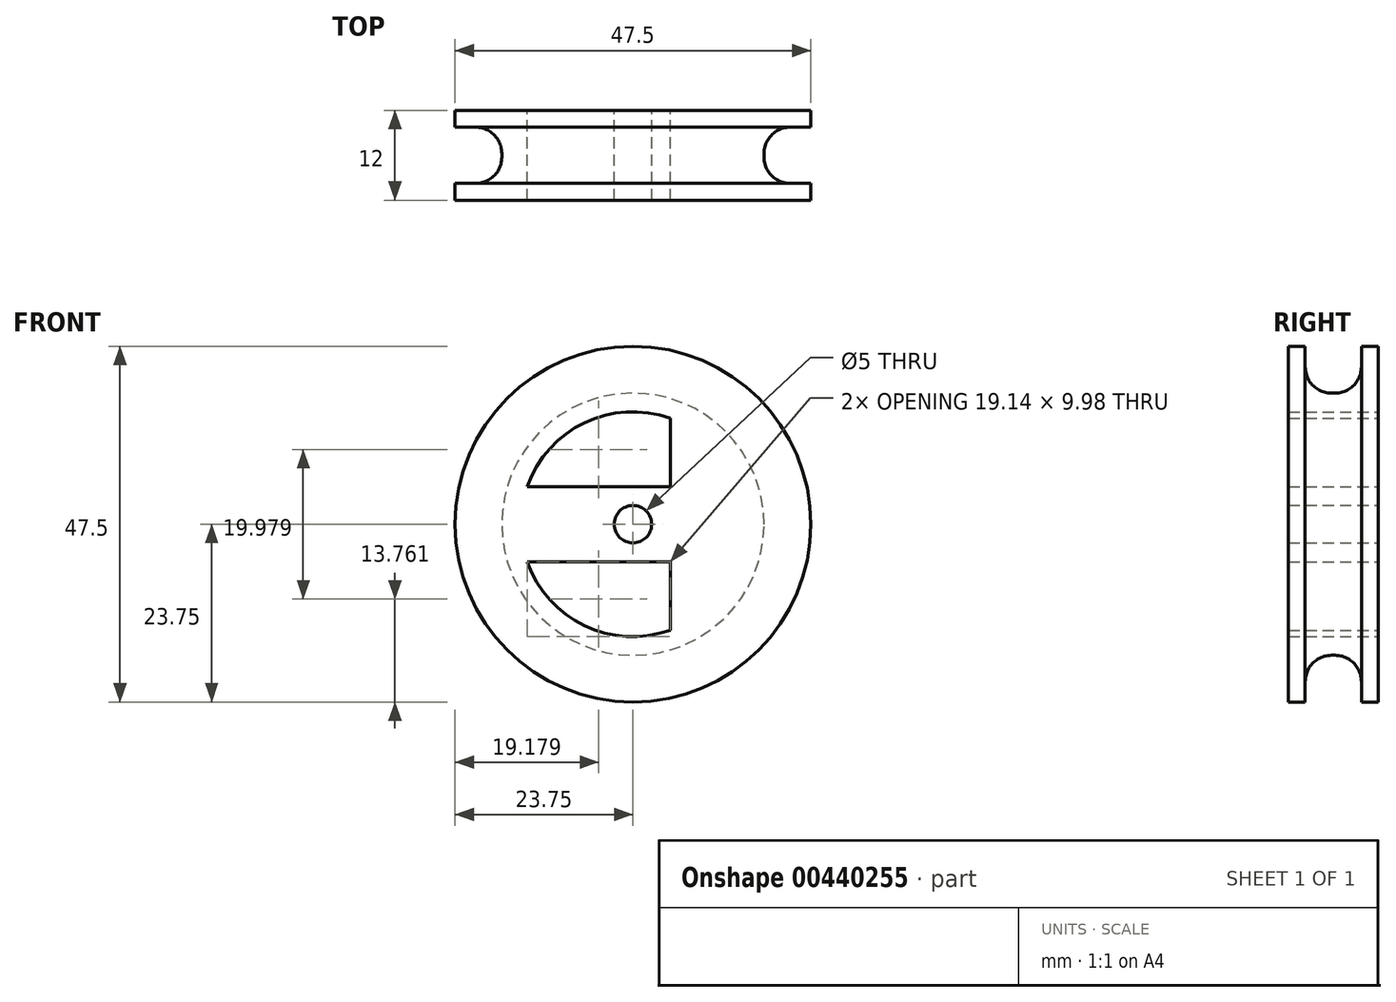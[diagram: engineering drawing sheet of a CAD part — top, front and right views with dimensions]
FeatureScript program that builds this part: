
annotation { "Feature Type Name" : "Feature", "Feature Type Description" : "" }
export const myFeature = defineFeature(function(context is Context, id is Id, definition is map)
    precondition{}
    {
        {
            var Q0;
            Q0=qCreatedBy(makeId("Front.planeOp"),FACE);
            var sketch = newSketch(context, id + "F0", { "sketchPlane" : qUnion([Q0])});
            skCircle(sketch, "E0", {"center": v(0, 0) * mm, "radius": 23.75 * mm});
            skCircle(sketch, "E1", {"center": v(0, 0) * mm, "radius": 15 * mm});
            skLineSegment(sketch, "E2", {"start": v(5, 14.14) * mm, "end": v(5, -14.14) * mm});
            skLineSegment(sketch, "E3", {"start": v(-5, 14.14) * mm, "end": v(-5, -14.14) * mm});
            skLineSegment(sketch, "E4", {"start": v(14.14, 5) * mm, "end": v(-14.14, 5) * mm});
            skLineSegment(sketch, "E5", {"start": v(14.14, -5) * mm, "end": v(-14.14, -5) * mm});
            skSolve(sketch);
        }
        {
            var Q0;
            Q0=qCreatedBy(makeId("Right.planeOp"),FACE);
            var sketch = newSketch(context, id + "F1", { "sketchPlane" : qUnion([Q0])});
            skLineSegment(sketch, "E6.bottom", {"start": v(3.75, 25) * mm, "end": v(-3.75, 25) * mm});
            skLineSegment(sketch, "E6.top", {"start": v(0.25, 17.5) * mm, "end": v(-0.25, 17.5) * mm});
            skLineSegment(sketch, "E6.left", {"start": v(3.75, 25) * mm, "end": v(3.75, 21) * mm});
            skLineSegment(sketch, "E6.right", {"start": v(-3.75, 25) * mm, "end": v(-3.75, 21) * mm});
            skPoint(sketch, "E7.visualSharp", {"position": v(-3.75, 17.5) * mm});
            skArc(sketch, "E7.filletArc", {"start": v(-3.75, 21) * mm, "mid": v(-2.72, 18.53) * mm, "end": v(-0.25, 17.5) * mm});
            skPoint(sketch, "E8.visualSharp", {"position": v(3.75, 17.5) * mm});
            skArc(sketch, "E8.filletArc", {"start": v(0.25, 17.5) * mm, "mid": v(2.72, 18.53) * mm, "end": v(3.75, 21) * mm});
            skSolve(sketch);
        }
        {
            var Q0;
            Q0=qCreatedBy(makeId("Top.planeOp"),FACE);
            var sketch = newSketch(context, id + "F2", { "sketchPlane" : qUnion([Q0])});
            skLineSegment(sketch, "E9", {"start": v(0, 51.52) * mm, "end": v(0, -55.54) * mm});
            skSolve(sketch);
        }
        {
            var Q0;
            Q0=makeQuery(id+"F0.imprint","IMPRINT",FACE,{"disambiguationData":[TD([[makeQuery(id+"F0.imprint","IMPRINT",EDGE,{"derivedFrom":sQuery(id+"F0.wireOp",EDGE,"E0")}),1.0]])]});
            var Q1;
            {var subQ0=sQuery(id+"F0.wireOp",EDGE,"E2");var subQ1=sQuery(id+"F0.wireOp",EDGE,"E1");var subQ2=makeQuery(id+"F0.imprint","INTERSECT",VERTEX,{"disambiguationData":[OD(0.0)],"derivedFrom":[subQ1,subQ0]});Q1=makeQuery(id+"F0.imprint","IMPRINT",FACE,{"disambiguationData":[TD([[makeQuery(id+"F0.imprint","IMPRINT",EDGE,{"disambiguationData":[TD([[subQ2,-1.0]])],"derivedFrom":subQ1}),1.0]])]});}
            var Q2;
            {var subQ0=sQuery(id+"F0.wireOp",EDGE,"E4");var subQ1=sQuery(id+"F0.wireOp",EDGE,"E1");var subQ2=makeQuery(id+"F0.imprint","INTERSECT",VERTEX,{"disambiguationData":[OD(0.0)],"derivedFrom":[subQ1,subQ0]});Q2=makeQuery(id+"F0.imprint","IMPRINT",FACE,{"disambiguationData":[TD([[makeQuery(id+"F0.imprint","IMPRINT",EDGE,{"disambiguationData":[TD([[subQ2,1.0]])],"derivedFrom":subQ1}),1.0]])]});}
            var Q3;
            {var subQ0=sQuery(id+"F0.wireOp",EDGE,"E4");var subQ1=sQuery(id+"F0.wireOp",EDGE,"E2");var subQ2=makeQuery(id+"F0.imprint","INTERSECT",VERTEX,{"derivedFrom":[subQ1,subQ0]});Q3=makeQuery(id+"F0.imprint","IMPRINT",FACE,{"disambiguationData":[TD([[makeQuery(id+"F0.imprint","IMPRINT",EDGE,{"disambiguationData":[TD([[subQ2,-1.0]])],"derivedFrom":subQ1}),-1.0]])]});}
            var Q4;
            {var subQ0=sQuery(id+"F0.wireOp",EDGE,"E4");var subQ1=sQuery(id+"F0.wireOp",EDGE,"E1");var subQ2=makeQuery(id+"F0.imprint","INTERSECT",VERTEX,{"disambiguationData":[OD(1.0)],"derivedFrom":[subQ1,subQ0]});Q4=makeQuery(id+"F0.imprint","IMPRINT",FACE,{"disambiguationData":[TD([[makeQuery(id+"F0.imprint","IMPRINT",EDGE,{"disambiguationData":[TD([[subQ2,-1.0]])],"derivedFrom":subQ1}),1.0]])]});}
            var Q5;
            {var subQ0=sQuery(id+"F0.wireOp",EDGE,"E2");var subQ1=sQuery(id+"F0.wireOp",EDGE,"E1");var subQ2=makeQuery(id+"F0.imprint","INTERSECT",VERTEX,{"disambiguationData":[OD(1.0)],"derivedFrom":[subQ1,subQ0]});Q5=makeQuery(id+"F0.imprint","IMPRINT",FACE,{"disambiguationData":[TD([[makeQuery(id+"F0.imprint","IMPRINT",EDGE,{"disambiguationData":[TD([[subQ2,1.0]])],"derivedFrom":subQ1}),1.0]])]});}
            extrude(context, id + "F3", {"entities" : qUnion([Q0, Q1, Q2, Q3, Q4, Q5]), "endBound" : BoundingType.SYMMETRIC, "depth" : 12 * mm});
        }
        {
            var Q0;
            Q0=qSketchRegion(id+"F1",true);
            var Q1;
            Q1=sQuery(id+"F2.wireOp",EDGE,"E9");
            revolve(context, id + "F4", {"operationType" : NewBodyOperationType.REMOVE, "entities" : qUnion([Q0]), "axis" : qUnion([Q1]), "revolveType" : RevolveType.FULL});
        }
        {
            var Q0;
            Q0=qCreatedBy(makeId("Front.planeOp"),FACE);
            var sketch = newSketch(context, id + "F5", { "sketchPlane" : qUnion([Q0])});
            skCircle(sketch, "E10", {"center": v(0, 0) * mm, "radius": 2.5 * mm});
            skSolve(sketch);
        }
        {
            var Q0;
            Q0=qSketchRegion(id+"F5",true);
            extrude(context, id + "F6", {"entities" : qUnion([Q0]), "operationType" : NewBodyOperationType.REMOVE, "endBound" : BoundingType.SYMMETRIC, "depth" : 25 * mm});
        }
    });
